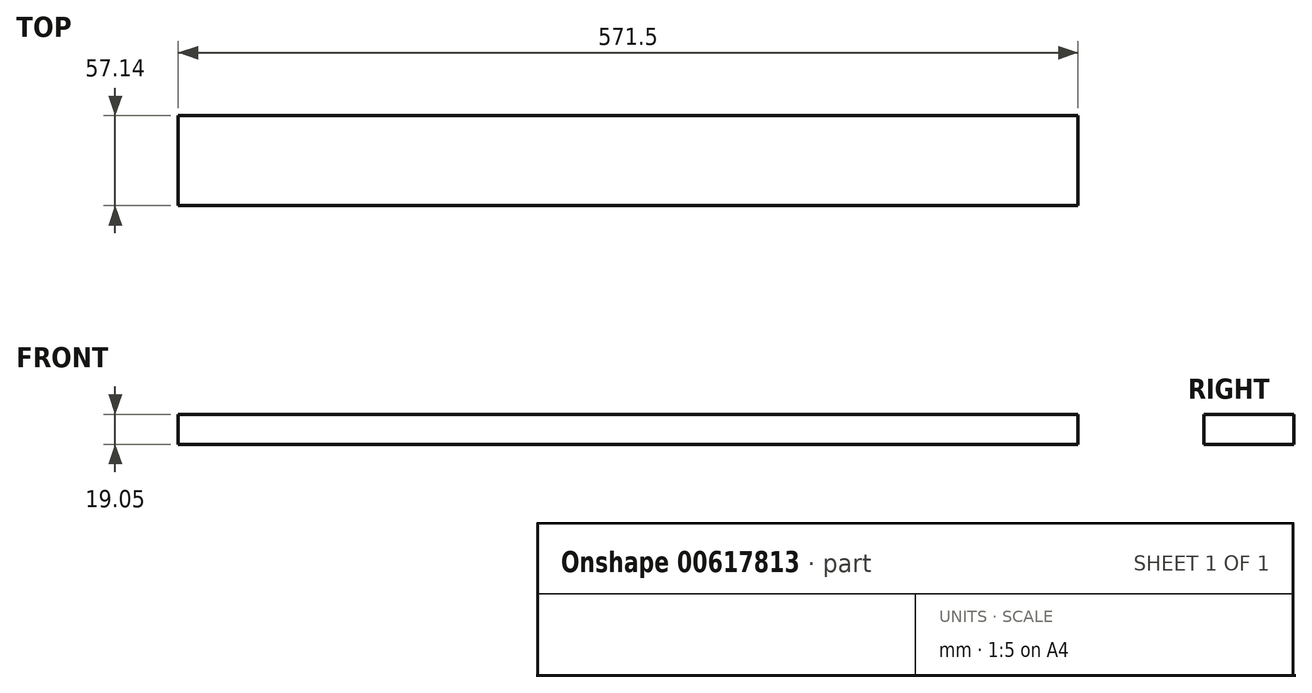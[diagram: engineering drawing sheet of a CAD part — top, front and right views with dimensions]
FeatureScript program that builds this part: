
annotation { "Feature Type Name" : "Feature", "Feature Type Description" : "" }
export const myFeature = defineFeature(function(context is Context, id is Id, definition is map)
    precondition{}
    {
        {
            var Q0;
            Q0=qCreatedBy(makeId("Top.planeOp"),FACE);
            var sketch = newSketch(context, id + "F0", { "sketchPlane" : qUnion([Q0])});
            skLineSegment(sketch, "E0.bottom", {"start": v(285.75, 28.57) * mm, "end": v(-285.75, 28.57) * mm});
            skLineSegment(sketch, "E0.top", {"start": v(285.75, -28.58) * mm, "end": v(-285.75, -28.58) * mm});
            skLineSegment(sketch, "E0.left", {"start": v(285.75, 28.57) * mm, "end": v(285.75, -28.58) * mm});
            skLineSegment(sketch, "E0.right", {"start": v(-285.75, 28.57) * mm, "end": v(-285.75, -28.58) * mm});
            skPoint(sketch, "E0.middle", {"position": v(0, 0) * mm});
            skSolve(sketch);
        }
        {
            var Q0;
            Q0=makeQuery(id+"F0.imprint","IMPRINT",FACE,{"disambiguationData":[TD([[makeQuery(id+"F0.imprint","IMPRINT",EDGE,{"derivedFrom":sQuery(id+"F0.wireOp",EDGE,"E0.bottom")}),1.0]])]});
            extrude(context, id + "F1", {"entities" : qUnion([Q0]), "depth" : 19.05 * mm, "offsetDistance" : 25.4 * mm});
        }
    });
